# Revit family: Soccer-Goal_Shootout-Portable-Round
name_source: partatom
category: Generic Models
revit_build: Autodesk Revit 2018 (Build: 20180423_1000(x64)
units: mm (PartAtom-declared; Revit-internal decimal feet)

## family parameters
Always vertical = Yes
Can host rebar = No
Cut with Voids When Loaded = No
OmniClass Number = 23.40.50.34.14
OmniClass Title = Gymnasium Equipment
Part Type = Normal
Room Calculation Point = No
Round Connector Dimension = Use Diameter
Shared = No
Work Plane-Based = No

## types (6) — shared parameters
Ballasts = Ballasts - Sandbag
Building Codes = https://www.brpbybison.com
Construction Details = https://www.arcat.com
Description = IPI by Bison Gymnasium Equipment
Frame Material = Aluminum
Green Building-LEED = https://www.arcat.com
Installation-Fabrication = http://www.ipibybison.com
Keynote = 11 66 00
Manufacturer = BRP by bison
Manufacturer Fax = 888-438-5312
Manufacturer Website = http://www.ipibybison.com
Model = As Specified
Netting = Finish - IPI by Bison - White Netting
Product Data = http://www.arcat.com
Revision = R1_2018-09
Sales Information = http://www.ipibybison.com
Specification = https://www.arcat.com
Square Frame Color = Powder Coat - White
Test Data = http://www.ipibybison.com
Top Depth = 4' - 0"
URL = https://ipibybison.com

## per-type parameters (varying)
| type | Ballasted | Base Depth | Goal Clearance | Height |
| SC1865PA40E - Anchored | No | 6' - 6" | 18' - 6" | 6' - 6" |
| SC2480PA40E - Anchored | No | 10' - 0" | 24' - 0" | 8' - 0" |
| SC1865PA40NT - Ballasted | Yes | 6' - 6" | 18' - 6" | 6' - 6" |
| SC2170PA40E - Anchored | No | 7' - 0" | 21' - 0" | 6' - 6" |
| SC2170PA40NT - Ballasted | Yes | 7' - 0" | 21' - 0" | 6' - 6" |
| SC2480PA40NT - Ballasted | Yes | 10' - 0" | 24' - 0" | 6' - 6" |

## geometry (parser evidence)
native form markers: Sweep x2
no freeform markers — native parametric forms only
